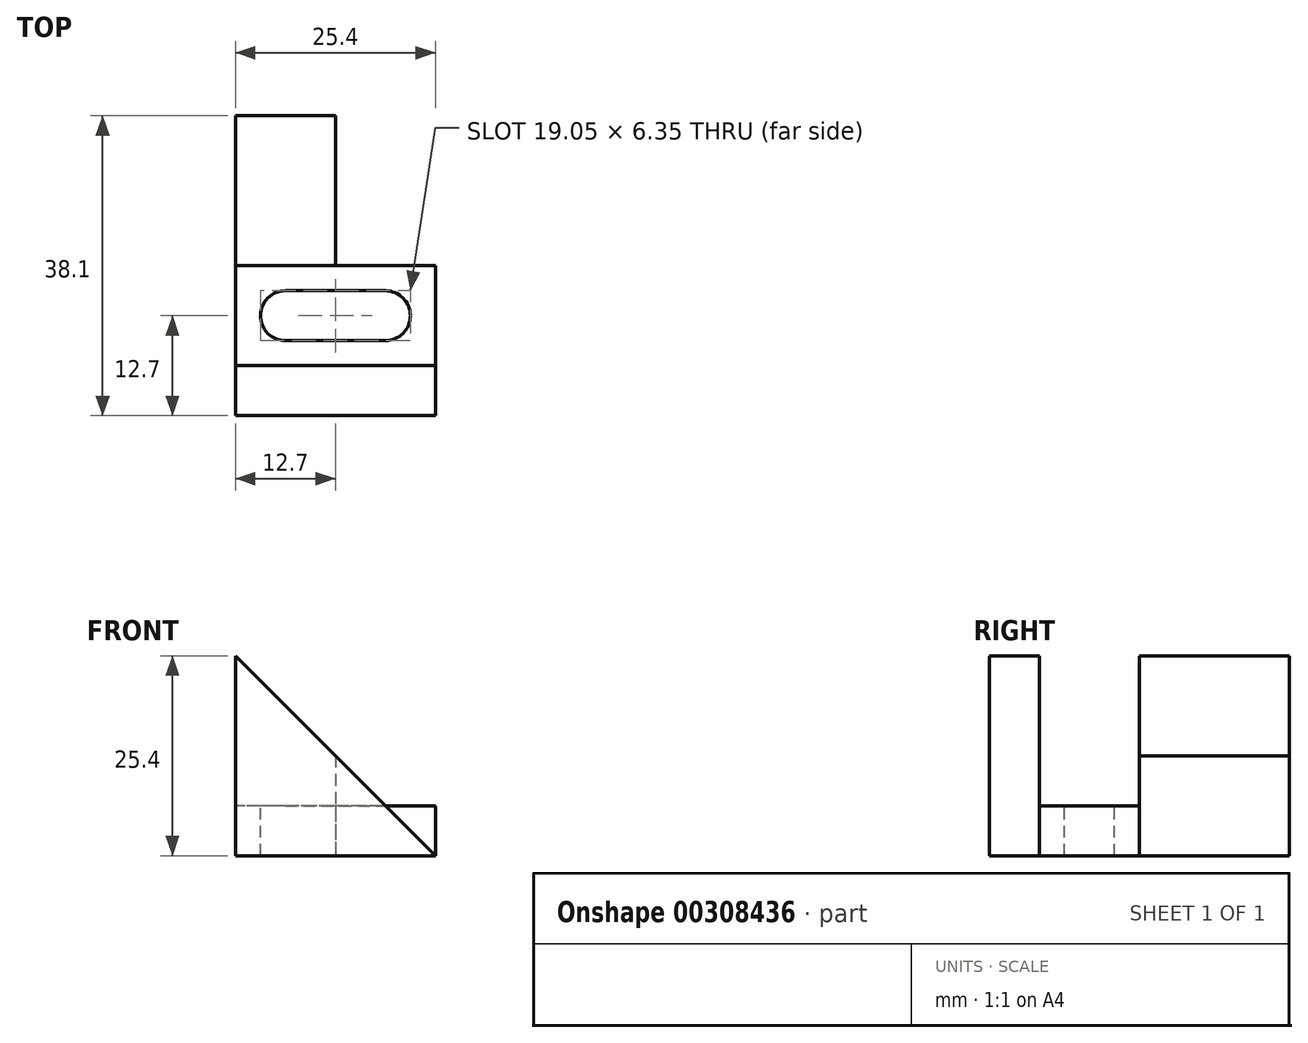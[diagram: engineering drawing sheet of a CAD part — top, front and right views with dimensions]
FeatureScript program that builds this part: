
annotation { "Feature Type Name" : "Feature", "Feature Type Description" : "" }
export const myFeature = defineFeature(function(context is Context, id is Id, definition is map)
    precondition{}
    {
        {
            var Q0;
            Q0=qCreatedBy(makeId("Front.planeOp"),FACE);
            var sketch = newSketch(context, id + "F0", { "sketchPlane" : qUnion([Q0])});
            skLineSegment(sketch, "E0", {"start": v(0, 0) * mm, "end": v(0, 25.4) * mm});
            skLineSegment(sketch, "E1", {"start": v(0, 0) * mm, "end": v(25.4, 0) * mm});
            skLineSegment(sketch, "E2", {"start": v(25.4, 0) * mm, "end": v(0, 25.4) * mm});
            skSolve(sketch);
        }
        {
            var Q0;
            Q0 = qSketchRegion(id + "F0", true);
            extrude(context, id + "F1", {"entities" : qUnion([Q0]), "depth" : 38.1 * mm});
        }
        {
            var Q0;
            Q0=makeQuery(id+"F1.opExtrude","SWEPT_FACE",FACE,{"disambiguationData":[OSD([sQuery(id+"F0.wireOp",EDGE,"E1")])]});
            var sketch = newSketch(context, id + "F2", { "sketchPlane" : qUnion([Q0])});
            skLineSegment(sketch, "E3.bottom", {"start": v(25.4, 19.05) * mm, "end": v(12.7, 19.05) * mm});
            skLineSegment(sketch, "E3.top", {"start": v(25.4, 0) * mm, "end": v(12.7, 0) * mm});
            skLineSegment(sketch, "E3.left", {"start": v(25.4, 19.05) * mm, "end": v(25.4, 0) * mm});
            skLineSegment(sketch, "E3.right", {"start": v(12.7, 19.05) * mm, "end": v(12.7, 0) * mm});
            skSolve(sketch);
        }
        {
            var Q0;
            Q0 = qSketchRegion(id + "F2", true);
            extrude(context, id + "F3", {"entities" : qUnion([Q0]), "operationType" : NewBodyOperationType.REMOVE, "endBound" : BoundingType.THROUGH_ALL, "oppositeDirection" : true, "depth" : 25.4 * mm});
        }
        {
            var Q0;
            Q0=makeQuery(id+"F1.opExtrude","SWEPT_FACE",FACE,{"disambiguationData":[OSD([sQuery(id+"F0.wireOp",EDGE,"E0")])]});
            var sketch = newSketch(context, id + "F4", { "sketchPlane" : qUnion([Q0])});
            skLineSegment(sketch, "E4", {"start": v(38.1, 25.4) * mm, "end": v(31.75, 25.4) * mm, "construction": true});
            skLineSegment(sketch, "E5.bottom", {"start": v(19.05, 25.4) * mm, "end": v(31.75, 25.4) * mm});
            skLineSegment(sketch, "E5.top", {"start": v(19.05, 6.35) * mm, "end": v(31.75, 6.35) * mm});
            skLineSegment(sketch, "E5.left", {"start": v(19.05, 25.4) * mm, "end": v(19.05, 6.35) * mm});
            skLineSegment(sketch, "E5.right", {"start": v(31.75, 25.4) * mm, "end": v(31.75, 6.35) * mm});
            skSolve(sketch);
        }
        {
            var Q0;
            Q0 = qSketchRegion(id + "F4", true);
            extrude(context, id + "F5", {"entities" : qUnion([Q0]), "operationType" : NewBodyOperationType.REMOVE, "endBound" : BoundingType.THROUGH_ALL, "oppositeDirection" : true, "depth" : 25.4 * mm});
        }
        {
            var Q0;
            Q0=makeQuery(id+"F3.boolean.opBoolean","COPY",FACE,{"derivedFrom":makeQuery(id+"F3.opExtrude","SWEPT_FACE",FACE,{"disambiguationData":[OSD([sQuery(id+"F2.wireOp",EDGE,"E3.bottom")])]})});
            var sketch = newSketch(context, id + "F6", { "sketchPlane" : qUnion([Q0])});
            skLineSegment(sketch, "E6", {"start": v(-19.05, 6.35) * mm, "end": v(-25.4, 6.35) * mm});
            skLineSegment(sketch, "E7", {"start": v(-25.4, 6.35) * mm, "end": v(-25.4, 0) * mm});
            skSolve(sketch);
        }
        {
            var Q0;
            Q0=makeQuery(id+"F6.imprint","IMPRINT",FACE,{"disambiguationData":[TD([[makeQuery(id+"F6.imprint","IMPRINT",EDGE,{"derivedFrom":sQuery(id+"F6.wireOp",EDGE,"E6")}),1.0]])]});
            extrude(context, id + "F7", {"entities" : qUnion([Q0]), "operationType" : NewBodyOperationType.ADD, "oppositeDirection" : true, "depth" : 12.7 * mm});
        }
        {
            var Q0;
            Q0=makeQuery(id+"F7.boolean.opBoolean","MERGE",FACE,{"derivedFrom":[makeQuery(id+"F5.boolean.opBoolean","COPY",FACE,{"derivedFrom":makeQuery(id+"F5.opExtrude","SWEPT_FACE",FACE,{"disambiguationData":[OSD([sQuery(id+"F4.wireOp",EDGE,"E5.top")])]})}),makeQuery(id+"F7.opExtrude","SWEPT_FACE",FACE,{"disambiguationData":[OSD([sQuery(id+"F6.wireOp",EDGE,"E6")])]})]});
            var sketch = newSketch(context, id + "F8", { "sketchPlane" : qUnion([Q0])});
            skLineSegment(sketch, "E8", {"start": v(0, -25.4) * mm, "end": v(6.35, -25.4) * mm, "construction": true});
            skLineSegment(sketch, "E9", {"start": v(6.35, -28.57) * mm, "end": v(19.05, -28.57) * mm});
            skArc(sketch, "E10", {"start": v(6.35, -28.57) * mm, "mid": v(4.1, -27.65) * mm, "end": v(3.18, -25.4) * mm});
            skLineSegment(sketch, "E11", {"start": v(25.4, -25.4) * mm, "end": v(19.05, -25.4) * mm, "construction": true});
            skArc(sketch, "E12", {"start": v(19.05, -28.57) * mm, "mid": v(21.3, -27.65) * mm, "end": v(22.23, -25.4) * mm});
            skArc(sketch, "E13.MirrorCS", {"start": v(6.35, -22.23) * mm, "mid": v(4.1, -23.15) * mm, "end": v(3.18, -25.4) * mm});
            skArc(sketch, "E14.MirrorCS", {"start": v(19.05, -22.23) * mm, "mid": v(21.3, -23.15) * mm, "end": v(22.23, -25.4) * mm});
            skLineSegment(sketch, "E15.MirrorCS", {"start": v(6.35, -22.23) * mm, "end": v(19.05, -22.23) * mm});
            skSolve(sketch);
        }
        {
            var Q0;
            Q0 = qSketchRegion(id + "F8", true);
            extrude(context, id + "F9", {"entities" : qUnion([Q0]), "operationType" : NewBodyOperationType.REMOVE, "endBound" : BoundingType.THROUGH_ALL, "oppositeDirection" : true, "depth" : 25.4 * mm});
        }
    });
